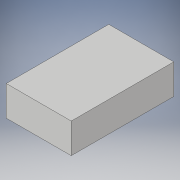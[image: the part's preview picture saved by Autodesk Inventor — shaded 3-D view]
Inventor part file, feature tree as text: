
AUTODESK INVENTOR PART (.ipt)
format: ipt  version: 2018 (Build 220112000, 112)  size: 87,040 bytes
history: native  units: in
note: dims shown in document units (in); Inventor stores cm internally (conversion verified against a paired STEP export)
features: extrude x1, sketch x1
ambient origin geometry x8: Origin, YZ Plane, XZ Plane, XY Plane, X Axis, Y Axis, Z Axis, Center Point
bodies: Solid1 (feature_tree)
feature tree (2):
  extrude  "Extrusion1"  Depth=10.25in
  sketch  "Sketch1"  dims[d0=6.5in d1=10.25in d2=3.0in d3=0.0in]
